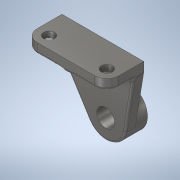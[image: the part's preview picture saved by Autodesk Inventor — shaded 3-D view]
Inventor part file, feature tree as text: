
AUTODESK INVENTOR PART (.ipt)
format: ipt  version: 2020 (Build 240168000, 168)  size: 329,728 bytes
history: native  units: mm
features: extrude x5, sketch x4, fillet x2, plane x1, rib x1
ambient origin geometry x8: Origin, YZ Plane, XZ Plane, XY Plane, X Axis, Y Axis, Z Axis, Center Point
bodies: Solid1 (feature_tree)
feature tree (13):
  extrude  "Extrusion1"  Depth=41.0mm
  sketch  "Sketch2"  dims[d2=18.0mm d3=22.0mm d4=0.0mm]
  extrude  "Extrusion2"  Depth=22.0mm TaperAngle=0.0deg
  extrude  "Extrusion3"  Depth=10.0mm
  plane  "Work Plane1"
  rib  "Rib1"
  sketch  "Sketch6"  dims[d8=10.0mm d9=0.0mm d10=27.0mm d11=0.0mm d12=-41.0mm d17=1.0mm d18=10.0mm d19=0.0mm d20=0.0mm d21=1.0mm d22=1.0mm d23=11.0mm d24=22.0mm d25=22.0mm d26=11.0mm d27=12.0mm d28=12.0mm d29=12.0mm d30=12.0mm d31=27.0mm d32=0.0mm d33=4.0mm d34=0.0mm d35=12.0mm d37=2.0mm d38=48.0mm d40=53.861561mm]
  extrude  "Extrusion4"  Depth=2.0mm TaperAngle=0.0deg
  extrude  "Extrusion5"  [1 undecoded]
  fillet  "Fillet1"  Radius=1.0mm
  fillet  "Fillet3"  Radius=11.0mm
  sketch  "Sketch1"  dims[d0=40.0mm d1=41.0mm]
  sketch  "Sketch5"  dims[d5=82.0mm d7=10.0mm]
note: 1 required parameter value undecoded (feature->parameter linkage not recoverable at this tier; creation-order binding heuristic only, values carry confidence <= 0.55)
